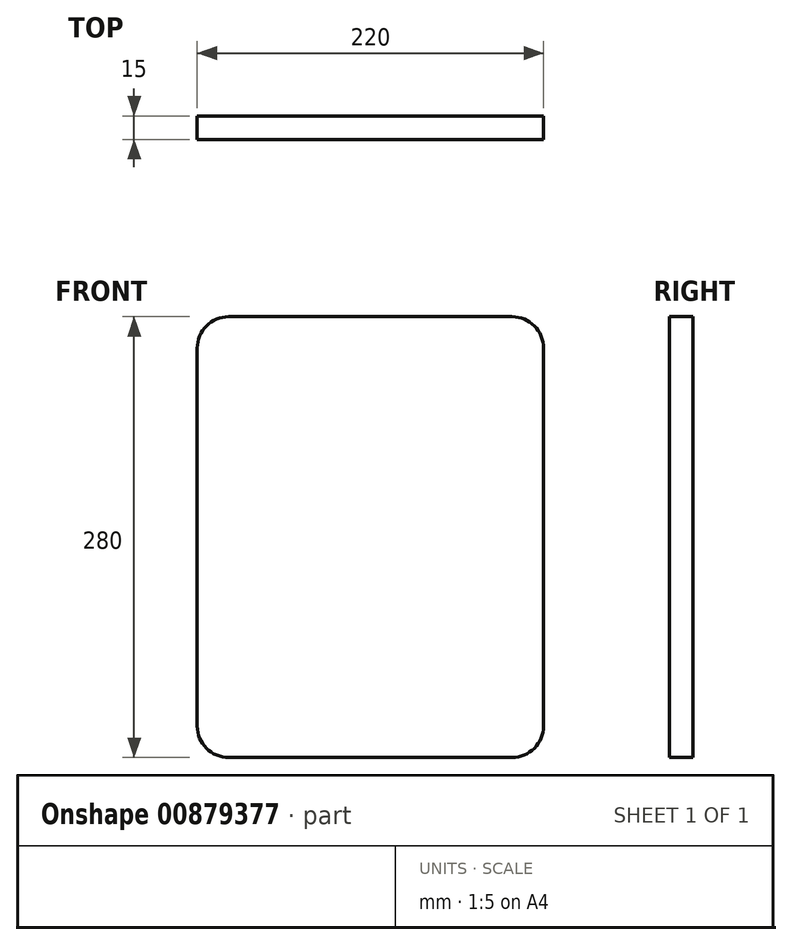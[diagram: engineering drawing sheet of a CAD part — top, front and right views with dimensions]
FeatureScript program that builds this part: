
annotation { "Feature Type Name" : "Feature", "Feature Type Description" : "" }
export const myFeature = defineFeature(function(context is Context, id is Id, definition is map)
    precondition{}
    {
        {
            var Q0;
            Q0=qCreatedBy(makeId("Front.planeOp"),FACE);
            var sketch = newSketch(context, id + "F0", { "sketchPlane" : qUnion([Q0])});
            skLineSegment(sketch, "E0.bottom", {"start": v(102.22, 153.33) * mm, "end": v(-77.78, 153.33) * mm});
            skLineSegment(sketch, "E0.top", {"start": v(102.22, -126.67) * mm, "end": v(-77.78, -126.67) * mm});
            skLineSegment(sketch, "E0.left", {"start": v(122.22, 133.33) * mm, "end": v(122.22, -106.67) * mm});
            skLineSegment(sketch, "E0.right", {"start": v(-97.78, -106.65) * mm, "end": v(-97.78, -106.67) * mm});
            skArc(sketch, "E1.filletArc", {"start": v(-77.78, 153.33) * mm, "mid": v(-91.92, 147.47) * mm, "end": v(-97.78, 133.33) * mm});
            skArc(sketch, "E2.filletArc", {"start": v(122.22, 133.33) * mm, "mid": v(116.36, 147.47) * mm, "end": v(102.22, 153.33) * mm});
            skArc(sketch, "E3.filletArc", {"start": v(102.22, -126.67) * mm, "mid": v(116.36, -120.81) * mm, "end": v(122.22, -106.67) * mm});
            skArc(sketch, "E4.filletArc", {"start": v(-97.78, -106.67) * mm, "mid": v(-91.92, -120.81) * mm, "end": v(-77.78, -126.67) * mm});
            skLineSegment(sketch, "E5", {"start": v(-97.78, -106.65) * mm, "end": v(-97.78, 133.33) * mm});
            skSolve(sketch);
        }
        {
            var Q0;
            Q0=makeQuery(id+"F0.imprint","IMPRINT",FACE,{"disambiguationData":[TD([[makeQuery(id+"F0.imprint","IMPRINT",EDGE,{"derivedFrom":sQuery(id+"F0.wireOp",EDGE,"E0.bottom")}),1.0]])]});
            extrude(context, id + "F1", {"entities" : qUnion([Q0]), "oppositeDirection" : true, "depth" : 15 * mm, "offsetDistance" : 25 * mm});
        }
    });
